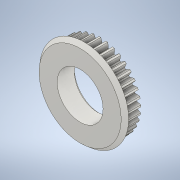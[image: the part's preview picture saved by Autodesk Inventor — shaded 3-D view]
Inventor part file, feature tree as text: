
AUTODESK INVENTOR PART (.ipt)
format: ipt  version: 2022 (Build 260153000, 153)  size: 1,195,520 bytes
history: native  units: mm (DEFAULTED — no unit token found)
features: sketch x4, plane x3, other x3, extrude x2, chamfer x1, revolve x1
ambient origin geometry x8: Origin, YZ Plane, XZ Plane, XY Plane, X Axis, Y Axis, Z Axis, Center Point
bodies: Solid1 (feature_tree)
feature tree (14):
  extrude  "Extrusion1"  Depth=9.525mm TaperAngle=0.0deg
  plane  "Work Plane1"
  plane  "Work Plane2"
  plane  "Work Plane3"
  other  "Spur Gear"
  extrude  "Extrusion2"  Depth=76.2mm TaperAngle=0.0deg
  chamfer  "Chamfer1"  Distance=0.849079mm
  revolve  "Revolution1"  [1 undecoded]
  sketch  "Sketch1"  dims[d0=39.506688mm d1=9.525mm d2=0.0mm]
  sketch  "Sketch2"  dims[d3=37.0mm d4=76.2mm d5=0.0mm d6=0.0mm d7=0.849079mm]
  other  "Srf1"
  sketch  "Sketch3"  dims[d9=0.0mm d14=0.0mm d15=23.753344mm]
  sketch  "Sketch4"  dims[d16=0.0mm d17=0.0mm d18=0.0mm d19=23.753344mm d20=22.1mm d21=0.0mm d22=0.0mm d23=1.2mm d24=3.175mm d25=45.0deg d26=35.0mm d27=6.35mm d30=3.175mm d31=19.75mm d32=360.0deg d33=22.68928mm d34=1.2mm]
  other  "Pitch Diameter"
note: 1 required parameter value undecoded (feature->parameter linkage not recoverable at this tier; creation-order binding heuristic only, values carry confidence <= 0.55)
